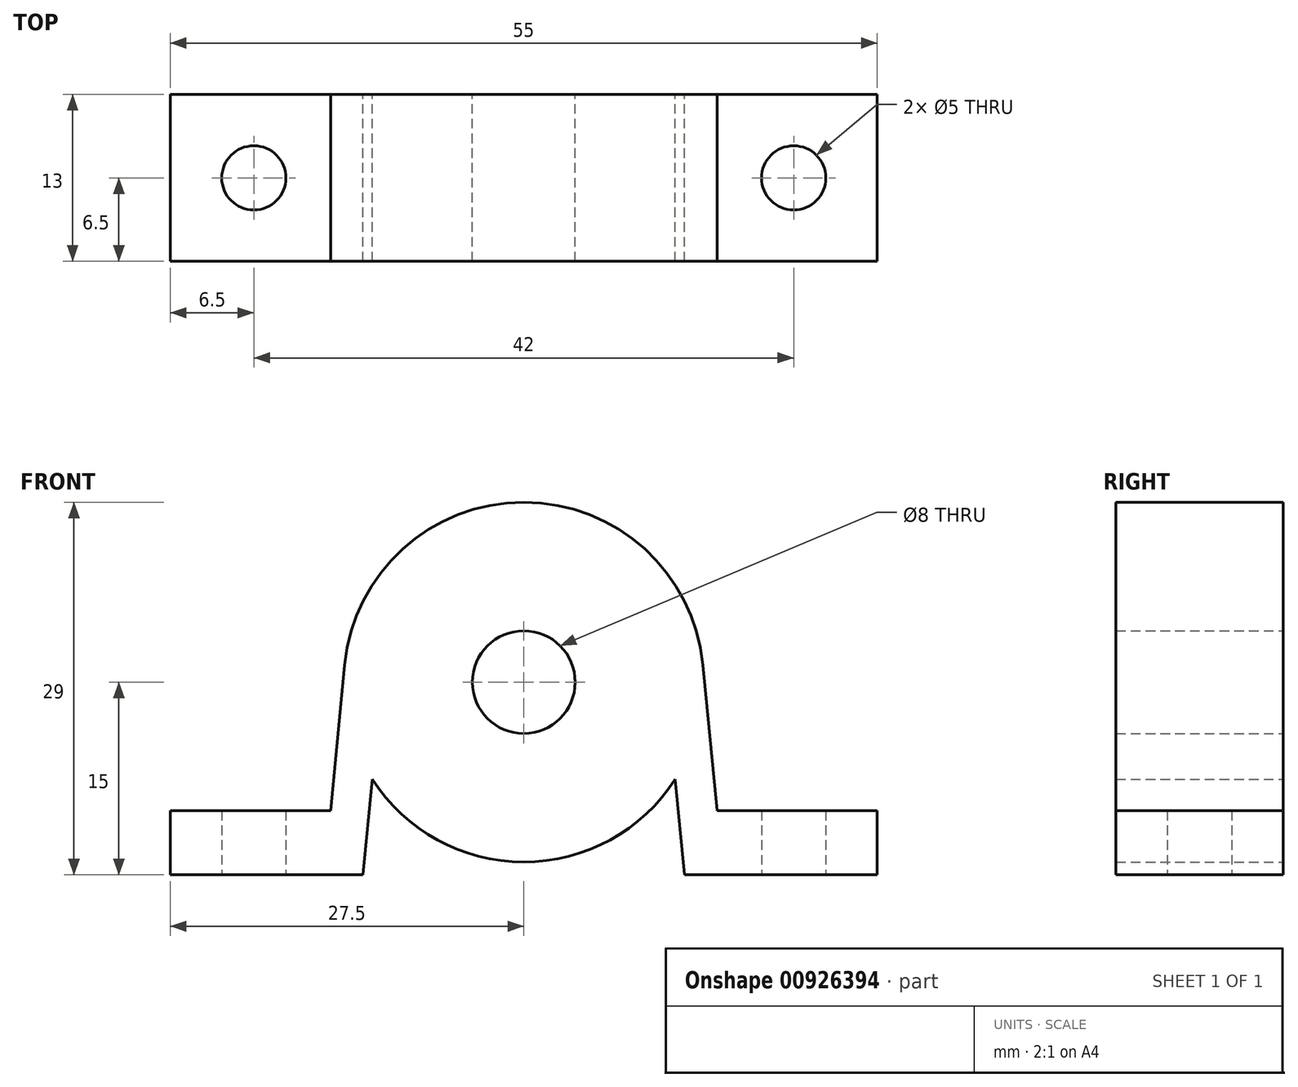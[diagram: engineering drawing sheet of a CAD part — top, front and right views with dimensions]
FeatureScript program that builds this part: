
annotation { "Feature Type Name" : "Feature", "Feature Type Description" : "" }
export const myFeature = defineFeature(function(context is Context, id is Id, definition is map)
    precondition{}
    {
        {
            var Q0;
            Q0=qCreatedBy(makeId("Front.planeOp"),FACE);
            var sketch = newSketch(context, id + "F0", { "sketchPlane" : qUnion([Q0])});
            skArc(sketch, "E0", {"start": v(0, 1) * mm, "mid": v(6.71, 2.71) * mm, "end": v(11.78, 7.44) * mm});
            skLineSegment(sketch, "E1", {"start": v(11.78, 7.44) * mm, "end": v(12.5, 0) * mm});
            skLineSegment(sketch, "E2", {"start": v(12.5, 0) * mm, "end": v(27.5, 0) * mm});
            skLineSegment(sketch, "E3", {"start": v(27.5, 0) * mm, "end": v(27.5, 5) * mm});
            skLineSegment(sketch, "E4", {"start": v(27.5, 5) * mm, "end": v(15.03, 5) * mm});
            skLineSegment(sketch, "E5", {"start": v(15.03, 5) * mm, "end": v(13.94, 16.35) * mm});
            skArc(sketch, "E6", {"start": v(13.94, 16.35) * mm, "mid": v(9.41, 25.36) * mm, "end": v(0, 29) * mm});
            skLineSegment(sketch, "E7", {"start": v(0, 29) * mm, "end": v(0, 0) * mm, "construction": true});
            skArc(sketch, "E8.MirrorCS", {"start": v(-13.94, 16.35) * mm, "mid": v(-9.41, 25.36) * mm, "end": v(0, 29) * mm});
            skLineSegment(sketch, "E9.MirrorCS", {"start": v(-27.5, 5) * mm, "end": v(-15.03, 5) * mm});
            skLineSegment(sketch, "E10.MirrorCS", {"start": v(-27.5, 0) * mm, "end": v(-27.5, 5) * mm});
            skLineSegment(sketch, "E11.MirrorCS", {"start": v(-11.78, 7.44) * mm, "end": v(-12.5, 0) * mm});
            skLineSegment(sketch, "E12.MirrorCS", {"start": v(-15.03, 5) * mm, "end": v(-13.94, 16.35) * mm});
            skLineSegment(sketch, "E13.MirrorCS", {"start": v(-12.5, 0) * mm, "end": v(-27.5, 0) * mm});
            skArc(sketch, "E14.MirrorCS", {"start": v(0, 1) * mm, "mid": v(-6.71, 2.71) * mm, "end": v(-11.78, 7.44) * mm});
            skCircle(sketch, "E15", {"center": v(0, 15) * mm, "radius": 4 * mm});
            skSolve(sketch);
        }
        {
            var Q0;
            Q0 = qSketchRegion(id + "F0", true);
            extrude(context, id + "F1", {"entities" : qUnion([Q0]), "depth" : 13 * mm, "offsetDistance" : 25 * mm});
        }
        {
            var Q0;
            Q0=makeQuery(id+"F1.opExtrude","SWEPT_FACE",FACE,{"disambiguationData":[OSD([sQuery(id+"F0.wireOp",EDGE,"E13.MirrorCS")])]});
            var sketch = newSketch(context, id + "F2", { "sketchPlane" : qUnion([Q0])});
            skCircle(sketch, "E16", {"center": v(-21, 6.5) * mm, "radius": 2.5 * mm});
            skLineSegment(sketch, "E17", {"start": v(0, 13) * mm, "end": v(0, 0) * mm, "construction": true});
            skCircle(sketch, "E18.MirrorC", {"center": v(21, 6.5) * mm, "radius": 2.5 * mm});
            skSolve(sketch);
        }
        {
            var Q0;
            Q0 = qSketchRegion(id + "F2", true);
            extrude(context, id + "F3", {"entities" : qUnion([Q0]), "operationType" : NewBodyOperationType.REMOVE, "endBound" : BoundingType.THROUGH_ALL, "oppositeDirection" : true, "depth" : 25 * mm, "offsetDistance" : 25 * mm});
        }
    });
